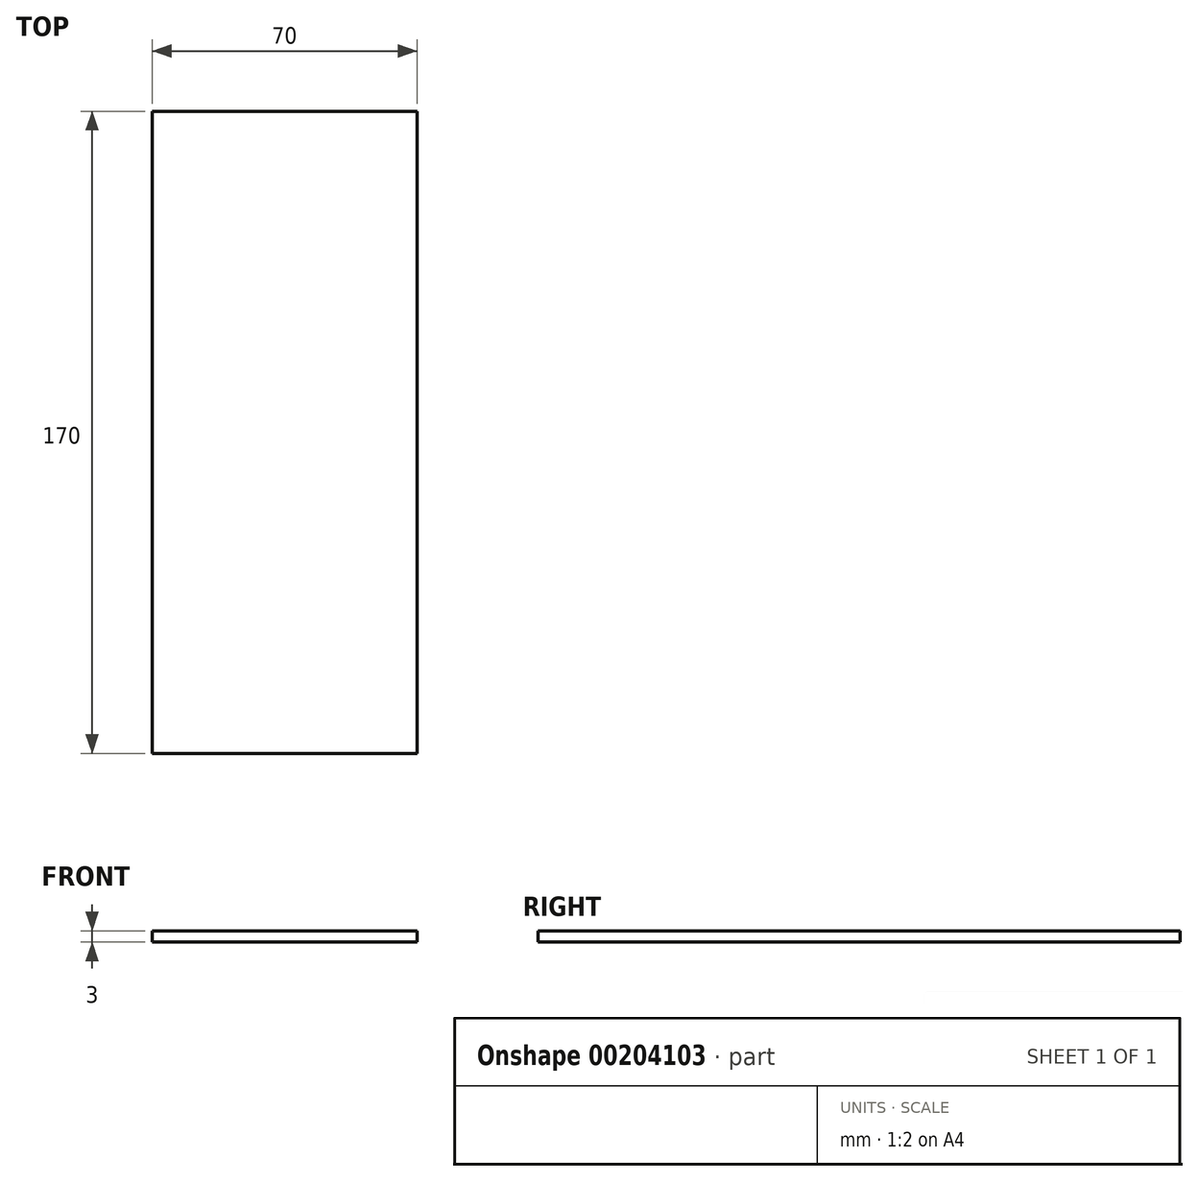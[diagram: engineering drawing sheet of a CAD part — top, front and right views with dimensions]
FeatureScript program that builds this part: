
annotation { "Feature Type Name" : "Feature", "Feature Type Description" : "" }
export const myFeature = defineFeature(function(context is Context, id is Id, definition is map)
    precondition{}
    {
        {
            var Q0;
            Q0=qCreatedBy(makeId("Top.planeOp"),FACE);
            var sketch = newSketch(context, id + "F0", { "sketchPlane" : qUnion([Q0])});
            skLineSegment(sketch, "E0.bottom", {"start": v(-35, -85) * mm, "end": v(35, -85) * mm});
            skLineSegment(sketch, "E0.top", {"start": v(-35, 85) * mm, "end": v(35, 85) * mm});
            skLineSegment(sketch, "E0.left", {"start": v(-35, -85) * mm, "end": v(-35, 85) * mm});
            skLineSegment(sketch, "E0.right", {"start": v(35, -85) * mm, "end": v(35, 85) * mm});
            skSolve(sketch);
        }
        {
            var Q0;
            Q0 = qSketchRegion(id + "F0", true);
            extrude(context, id + "F1", {"entities" : qUnion([Q0]), "depth" : 3 * mm});
        }
    });
